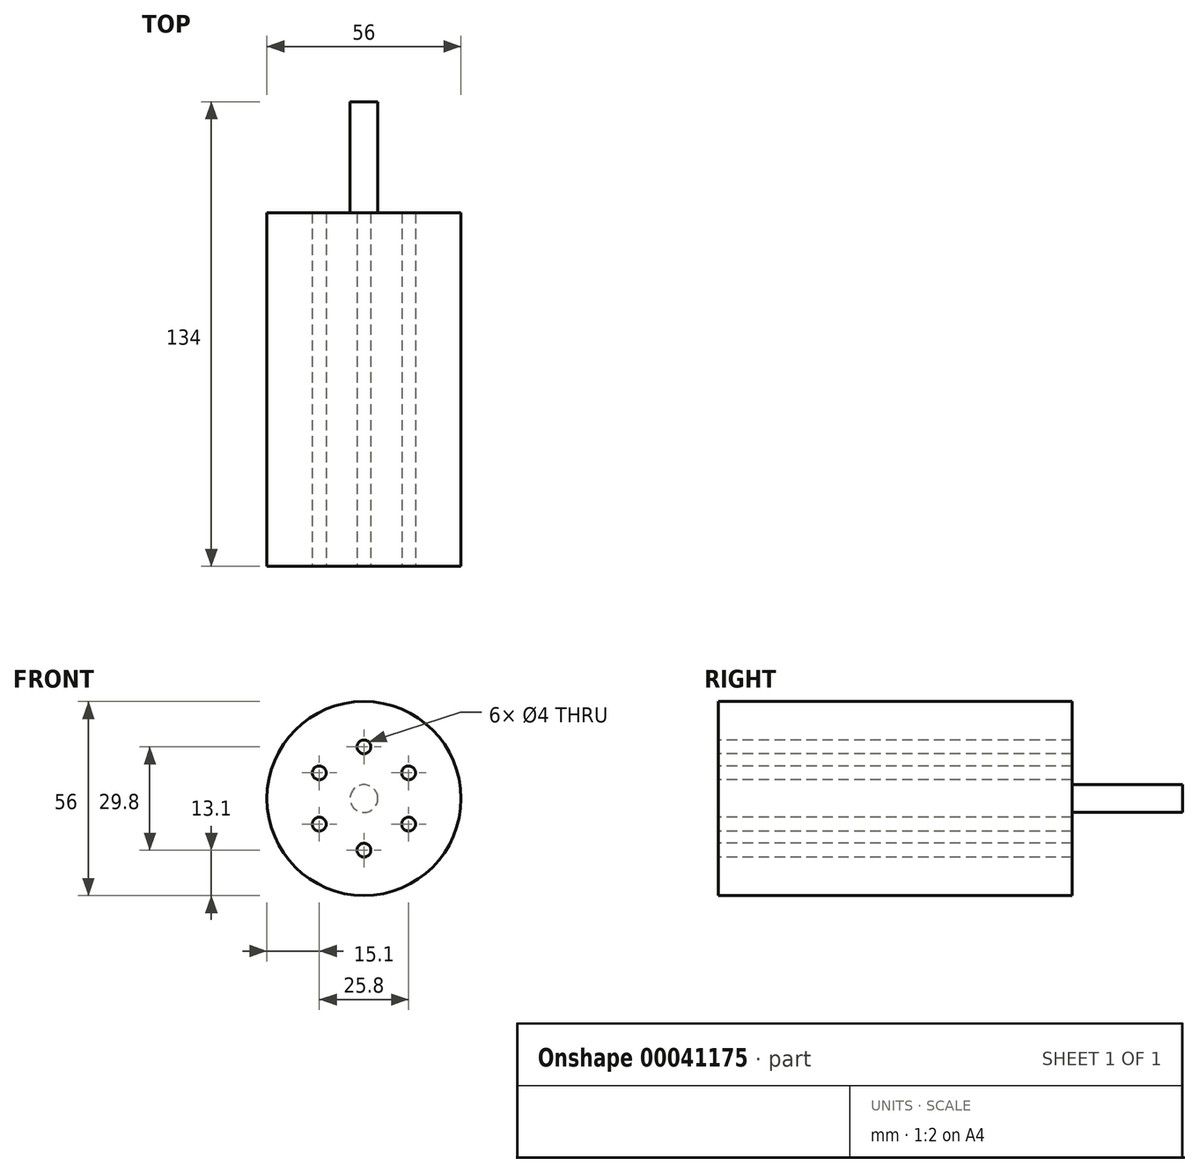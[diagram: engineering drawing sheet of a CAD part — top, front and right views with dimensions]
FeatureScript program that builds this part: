
annotation { "Feature Type Name" : "Feature", "Feature Type Description" : "" }
export const myFeature = defineFeature(function(context is Context, id is Id, definition is map)
    precondition{}
    {
        {
            var Q0;
            Q0=qCreatedBy(makeId("Front.planeOp"),FACE);
            var sketch = newSketch(context, id + "F0", { "sketchPlane" : qUnion([Q0])});
            skCircle(sketch, "E0", {"center": v(0, 0) * mm, "radius": 4 * mm});
            skCircle(sketch, "E1", {"center": v(0, 0) * mm, "radius": 28 * mm});
            skLineSegment(sketch, "E2", {"start": v(38.49, 0) * mm, "end": v(-45.93, 0) * mm, "construction": true});
            skLineSegment(sketch, "E3", {"start": v(39.25, 7.4) * mm, "end": v(-46.25, 7.4) * mm, "construction": true});
            skLineSegment(sketch, "E4", {"start": v(39.25, -7.4) * mm, "end": v(-46.25, -7.4) * mm, "construction": true});
            skLineSegment(sketch, "E5", {"start": v(0, 24.46) * mm, "end": v(0, -25) * mm, "construction": true});
            skLineSegment(sketch, "E6", {"start": v(12.9, 22.94) * mm, "end": v(12.9, -22.9) * mm, "construction": true});
            skLineSegment(sketch, "E7", {"start": v(-12.9, 22.94) * mm, "end": v(-12.9, 8.14) * mm, "construction": true});
            skLineSegment(sketch, "E8", {"start": v(35.9, -14.9) * mm, "end": v(-20.06, -14.9) * mm, "construction": true});
            skLineSegment(sketch, "E9.trimOffspring", {"start": v(35.9, 14.9) * mm, "end": v(-20.06, 14.9) * mm, "construction": true});
            skLineSegment(sketch, "E10.trimOffspring", {"start": v(-12.9, 7.4) * mm, "end": v(-12.9, -22.9) * mm, "construction": true});
            skCircle(sketch, "E11", {"center": v(0, 14.9) * mm, "radius": 2 * mm});
            skCircle(sketch, "E12", {"center": v(-12.9, 7.4) * mm, "radius": 2 * mm});
            skCircle(sketch, "E13", {"center": v(-12.9, -7.4) * mm, "radius": 2 * mm});
            skPoint(sketch, "E14", {"position": v(-12.9, -7.75) * mm});
            skCircle(sketch, "E15", {"center": v(0, -14.9) * mm, "radius": 2 * mm});
            skCircle(sketch, "E16", {"center": v(12.9, -7.4) * mm, "radius": 2 * mm});
            skCircle(sketch, "E17", {"center": v(12.9, 7.4) * mm, "radius": 2 * mm});
            skSolve(sketch);
        }
        {
            var Q0;
            Q0=makeQuery(id+"F0.imprint","IMPRINT",FACE,{"disambiguationData":[TD([[makeQuery(id+"F0.imprint","IMPRINT",EDGE,{"derivedFrom":sQuery(id+"F0.wireOp",EDGE,"E0")}),1.0]])]});
            extrude(context, id + "F1", {"entities" : qUnion([Q0]), "oppositeDirection" : true, "depth" : 134 * mm});
        }
        {
            var Q0;
            Q0=makeQuery(id+"F0.imprint","IMPRINT",FACE,{"disambiguationData":[TD([[makeQuery(id+"F0.imprint","IMPRINT",EDGE,{"derivedFrom":sQuery(id+"F0.wireOp",EDGE,"E0")}),-1.0]])]});
            extrude(context, id + "F2", {"entities" : qUnion([Q0]), "operationType" : NewBodyOperationType.ADD, "oppositeDirection" : true, "depth" : 102 * mm});
        }
    });
